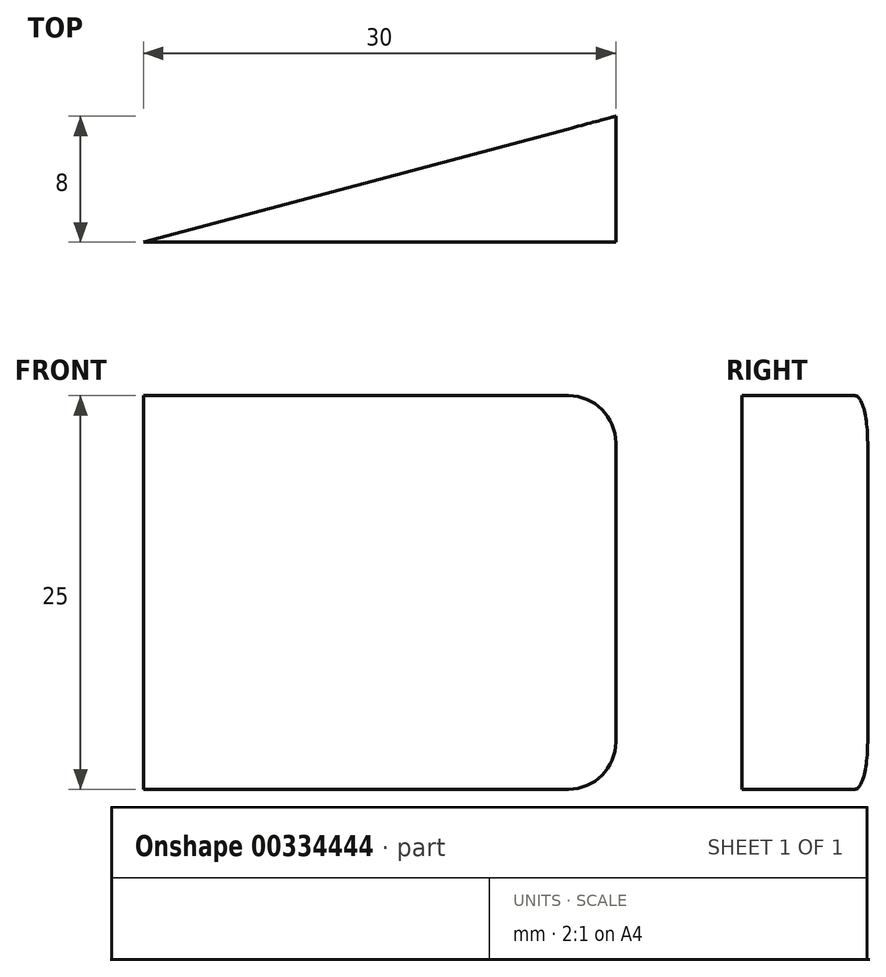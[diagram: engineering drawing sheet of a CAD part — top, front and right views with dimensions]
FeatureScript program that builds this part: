
annotation { "Feature Type Name" : "Feature", "Feature Type Description" : "" }
export const myFeature = defineFeature(function(context is Context, id is Id, definition is map)
    precondition{}
    {
        {
            var Q0;
            Q0=qCreatedBy(makeId("Top.planeOp"),FACE);
            var sketch = newSketch(context, id + "F0", { "sketchPlane" : qUnion([Q0])});
            skLineSegment(sketch, "E0", {"start": v(0, 0) * mm, "end": v(30, 0) * mm});
            skLineSegment(sketch, "E1", {"start": v(30, 0) * mm, "end": v(30, 8) * mm});
            skLineSegment(sketch, "E2", {"start": v(30, 8) * mm, "end": v(0, 0) * mm});
            skSolve(sketch);
        }
        {
            var Q0;
            Q0 = qSketchRegion(id + "F0", true);
            extrude(context, id + "F1", {"entities" : qUnion([Q0]), "depth" : 25 * mm});
        }
        {
            var Q0;
            Q0=makeQuery(id+"F1.opExtrude","CAP_EDGE",EDGE,{"disambiguationData":[OSD([sQuery(id+"F0.wireOp",EDGE,"E1")])],"isStart":false});
            var Q1;
            Q1=makeQuery(id+"F1.opExtrude","CAP_EDGE",EDGE,{"disambiguationData":[OSD([sQuery(id+"F0.wireOp",EDGE,"E1")])],"isStart":true});
            fillet(context, id + "F2", {"entities" : qUnion([Q0, Q1]), "radius" : 3 * mm, "tangentPropagation" : true, "allowEdgeOverflow" : false});
        }
    });
